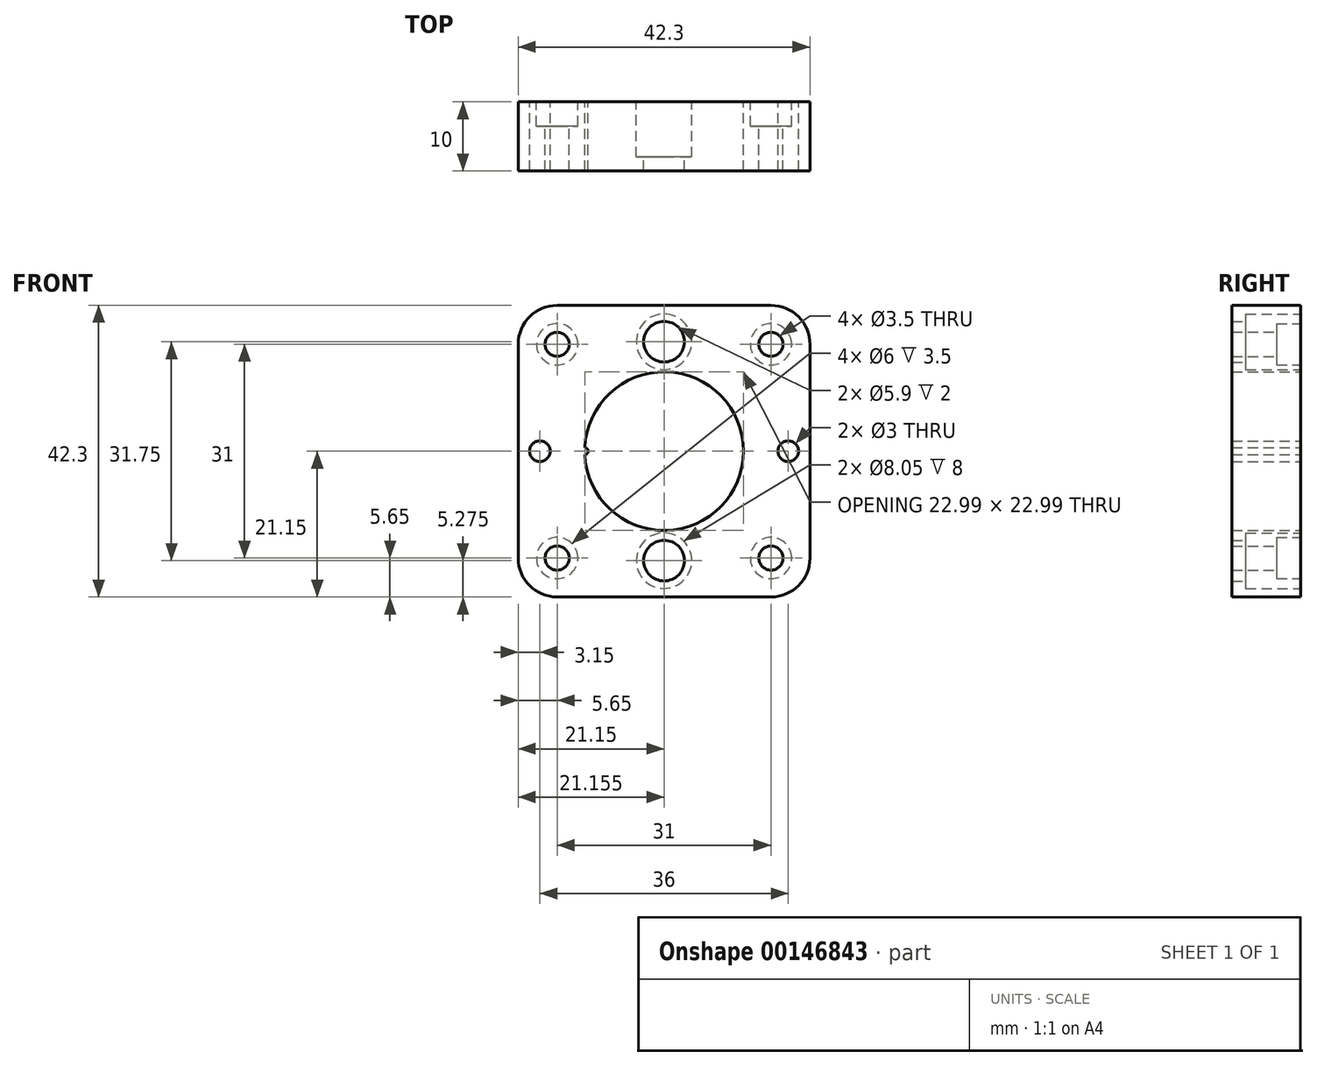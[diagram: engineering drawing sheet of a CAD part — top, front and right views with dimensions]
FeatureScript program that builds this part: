
annotation { "Feature Type Name" : "Feature", "Feature Type Description" : "" }
export const myFeature = defineFeature(function(context is Context, id is Id, definition is map)
    precondition{}
    {
        {
            var Q0;
            Q0=qCreatedBy(makeId("Front.planeOp"),FACE);
            var sketch = newSketch(context, id + "F0", { "sketchPlane" : qUnion([Q0])});
            skLineSegment(sketch, "E0.bottom", {"start": v(21.15, -21.15) * mm, "end": v(-21.15, -21.15) * mm});
            skLineSegment(sketch, "E0.top", {"start": v(21.15, 21.15) * mm, "end": v(-21.15, 21.15) * mm});
            skLineSegment(sketch, "E0.left", {"start": v(21.15, -21.15) * mm, "end": v(21.15, 21.15) * mm});
            skLineSegment(sketch, "E0.right", {"start": v(-21.15, -21.15) * mm, "end": v(-21.15, 21.15) * mm});
            skPoint(sketch, "E0.middle", {"position": v(0, 0) * mm});
            skLineSegment(sketch, "E1.bottom", {"start": v(15.5, 15.5) * mm, "end": v(-15.5, 15.5) * mm, "construction": true});
            skLineSegment(sketch, "E1.top", {"start": v(15.5, -15.5) * mm, "end": v(-15.5, -15.5) * mm, "construction": true});
            skLineSegment(sketch, "E1.left", {"start": v(15.5, 15.5) * mm, "end": v(15.5, -15.5) * mm, "construction": true});
            skLineSegment(sketch, "E1.right", {"start": v(-15.5, 15.5) * mm, "end": v(-15.5, -15.5) * mm, "construction": true});
            skCircle(sketch, "E2", {"center": v(-15.5, 15.5) * mm, "radius": 1.75 * mm});
            skCircle(sketch, "E3", {"center": v(15.5, 15.5) * mm, "radius": 1.75 * mm});
            skCircle(sketch, "E4", {"center": v(15.5, -15.5) * mm, "radius": 1.75 * mm});
            skCircle(sketch, "E5", {"center": v(-15.5, -15.5) * mm, "radius": 1.75 * mm});
            skCircle(sketch, "E6", {"center": v(0, 0) * mm, "radius": 11.5 * mm});
            skCircle(sketch, "E7", {"center": v(0, 0) * mm, "radius": 15.5 * mm, "construction": true});
            skCircle(sketch, "E8", {"center": v(0, 0) * mm, "radius": 9.5 * mm, "construction": true});
            skLineSegment(sketch, "E9.bottom", {"start": v(-18, 18) * mm, "end": v(18, 18) * mm, "construction": true});
            skLineSegment(sketch, "E9.top", {"start": v(-18, -18) * mm, "end": v(18, -18) * mm, "construction": true});
            skLineSegment(sketch, "E9.left", {"start": v(-18, 18) * mm, "end": v(-18, -18) * mm, "construction": true});
            skLineSegment(sketch, "E9.right", {"start": v(18, 18) * mm, "end": v(18, -18) * mm, "construction": true});
            skCircle(sketch, "E10", {"center": v(-18, 0) * mm, "radius": 1.5 * mm});
            skCircle(sketch, "E11", {"center": v(18, 0) * mm, "radius": 1.5 * mm});
            skLineSegment(sketch, "E12.bottom", {"start": v(-15.88, 15.88) * mm, "end": v(15.88, 15.88) * mm, "construction": true});
            skLineSegment(sketch, "E12.top", {"start": v(-15.88, -15.87) * mm, "end": v(15.88, -15.87) * mm, "construction": true});
            skLineSegment(sketch, "E12.left", {"start": v(-15.88, 15.88) * mm, "end": v(-15.88, -15.88) * mm, "construction": true});
            skLineSegment(sketch, "E12.right", {"start": v(15.88, 15.88) * mm, "end": v(15.87, -15.88) * mm, "construction": true});
            skCircle(sketch, "E13", {"center": v(0, 15.88) * mm, "radius": 2.95 * mm});
            skCircle(sketch, "E14", {"center": v(0, -15.87) * mm, "radius": 2.95 * mm});
            skSolve(sketch);
        }
        {
            var Q0;
            Q0=qSketchRegion(id+"F0",true);
            extrude(context, id + "F1", {"entities" : qUnion([Q0]), "depth" : 10 * mm});
        }
        {
            var Q0;
            Q0=makeQuery(id+"F1.opExtrude","CAP_FACE",FACE,{"disambiguationData":[OSD([sQuery(id+"F0.wireOp",EDGE,"E0.bottom"),sQuery(id+"F0.wireOp",EDGE,"E0.top"),sQuery(id+"F0.wireOp",EDGE,"E0.left"),sQuery(id+"F0.wireOp",EDGE,"E0.right"),sQuery(id+"F0.wireOp",EDGE,"E2"),sQuery(id+"F0.wireOp",EDGE,"E3"),sQuery(id+"F0.wireOp",EDGE,"E4"),sQuery(id+"F0.wireOp",EDGE,"E5"),sQuery(id+"F0.wireOp",EDGE,"E6")])],"isStart":true});
            var sketch = newSketch(context, id + "F2", { "sketchPlane" : qUnion([Q0])});
            skCircle(sketch, "E15", {"center": v(-15.5, 15.5) * mm, "radius": 3 * mm});
            skCircle(sketch, "E16", {"center": v(15.5, 15.5) * mm, "radius": 3 * mm});
            skCircle(sketch, "E17", {"center": v(15.5, -15.5) * mm, "radius": 3 * mm});
            skCircle(sketch, "E18", {"center": v(-15.5, -15.5) * mm, "radius": 3 * mm});
            skSolve(sketch);
        }
        {
            var Q0;
            Q0=qSketchRegion(id+"F2",true);
            extrude(context, id + "F3", {"entities" : qUnion([Q0]), "operationType" : NewBodyOperationType.REMOVE, "oppositeDirection" : true, "depth" : 3.5 * mm});
        }
        {
            var Q0;
            Q0=makeQuery(id+"F1.opExtrude","CAP_FACE",FACE,{"disambiguationData":[OSD([sQuery(id+"F0.wireOp",EDGE,"E0.bottom"),sQuery(id+"F0.wireOp",EDGE,"E0.top"),sQuery(id+"F0.wireOp",EDGE,"E0.left"),sQuery(id+"F0.wireOp",EDGE,"E0.right"),sQuery(id+"F0.wireOp",EDGE,"E2"),sQuery(id+"F0.wireOp",EDGE,"E3"),sQuery(id+"F0.wireOp",EDGE,"E4"),sQuery(id+"F0.wireOp",EDGE,"E5"),sQuery(id+"F0.wireOp",EDGE,"E6"),sQuery(id+"F0.wireOp",EDGE,"vDiBe0wF-wDsX-KkF6-MKLt-YGDdTFYj98wm"),sQuery(id+"F0.wireOp",EDGE,"E10"),sQuery(id+"F0.wireOp",EDGE,"xSFk8E4A-PhjX-R7jy-D4t1-Jk2nO5joamHX"),sQuery(id+"F0.wireOp",EDGE,"E11")])],"isStart":true});
            var sketch = newSketch(context, id + "F4", { "sketchPlane" : qUnion([Q0])});
            skLineSegment(sketch, "E19.bottom", {"start": v(15.88, 15.88) * mm, "end": v(-15.88, 15.88) * mm, "construction": true});
            skLineSegment(sketch, "E19.top", {"start": v(15.88, -15.88) * mm, "end": v(-15.88, -15.88) * mm, "construction": true});
            skLineSegment(sketch, "E19.left", {"start": v(15.88, 15.88) * mm, "end": v(15.88, -15.88) * mm, "construction": true});
            skLineSegment(sketch, "E19.right", {"start": v(-15.88, 15.88) * mm, "end": v(-15.88, -15.88) * mm, "construction": true});
            skPoint(sketch, "E19.middle", {"position": v(0, 0) * mm});
            skCircle(sketch, "E20", {"center": v(0, 15.88) * mm, "radius": 4.03 * mm});
            skCircle(sketch, "E21", {"center": v(0, -15.88) * mm, "radius": 4.03 * mm});
            skSolve(sketch);
        }
        {
            var Q0;
            Q0=qSketchRegion(id+"F4",true);
            extrude(context, id + "F5", {"entities" : qUnion([Q0]), "operationType" : NewBodyOperationType.REMOVE, "oppositeDirection" : true, "depth" : 8 * mm});
        }
        {
            var Q0;
            Q0=makeQuery(id+"F1.opExtrude","SWEPT_EDGE",EDGE,{"disambiguationData":[OSD([sQuery(id+"F0.wireOp",EDGE,"E0.top"),sQuery(id+"F0.wireOp",EDGE,"E0.left")])]});
            var Q1;
            Q1=makeQuery(id+"F1.opExtrude","SWEPT_EDGE",EDGE,{"disambiguationData":[OSD([sQuery(id+"F0.wireOp",EDGE,"E0.bottom"),sQuery(id+"F0.wireOp",EDGE,"E0.left")])]});
            var Q2;
            Q2=makeQuery(id+"F1.opExtrude","SWEPT_EDGE",EDGE,{"disambiguationData":[OSD([sQuery(id+"F0.wireOp",EDGE,"E0.top"),sQuery(id+"F0.wireOp",EDGE,"E0.right")])]});
            var Q3;
            Q3=makeQuery(id+"F1.opExtrude","SWEPT_EDGE",EDGE,{"disambiguationData":[OSD([sQuery(id+"F0.wireOp",EDGE,"E0.bottom"),sQuery(id+"F0.wireOp",EDGE,"E0.right")])]});
            fillet(context, id + "F6", {"entities" : qUnion([Q0, Q1, Q2, Q3]), "radius" : 5.65 * mm, "tangentPropagation" : true, "allowEdgeOverflow" : false});
        }
        {
            var Q0;
            Q0=makeQuery(id+"F1.opExtrude","CAP_FACE",FACE,{"disambiguationData":[OSD([sQuery(id+"F0.wireOp",EDGE,"E0.bottom"),sQuery(id+"F0.wireOp",EDGE,"E0.top"),sQuery(id+"F0.wireOp",EDGE,"E0.left"),sQuery(id+"F0.wireOp",EDGE,"E0.right"),sQuery(id+"F0.wireOp",EDGE,"E2"),sQuery(id+"F0.wireOp",EDGE,"E3"),sQuery(id+"F0.wireOp",EDGE,"E4"),sQuery(id+"F0.wireOp",EDGE,"E5"),sQuery(id+"F0.wireOp",EDGE,"E6"),sQuery(id+"F0.wireOp",EDGE,"E10"),sQuery(id+"F0.wireOp",EDGE,"E11"),sQuery(id+"F0.wireOp",EDGE,"E13"),sQuery(id+"F0.wireOp",EDGE,"E14")])],"isStart":true});
            var sketch = newSketch(context, id + "F7", { "sketchPlane" : qUnion([Q0])});
            skArc(sketch, "E22", {"start": v(11.49, 0.5) * mm, "mid": v(11, 0) * mm, "end": v(11.49, -0.5) * mm});
            skArc(sketch, "E23", {"start": v(11.49, -0.5) * mm, "mid": v(11.5, 0) * mm, "end": v(11.49, 0.5) * mm});
            skSolve(sketch);
        }
        {
            var Q0;
            Q0=qSketchRegion(id+"F7",true);
            extrude(context, id + "F8", {"entities" : qUnion([Q0]), "operationType" : NewBodyOperationType.ADD, "oppositeDirection" : true, "depth" : 10 * mm});
        }
    });
